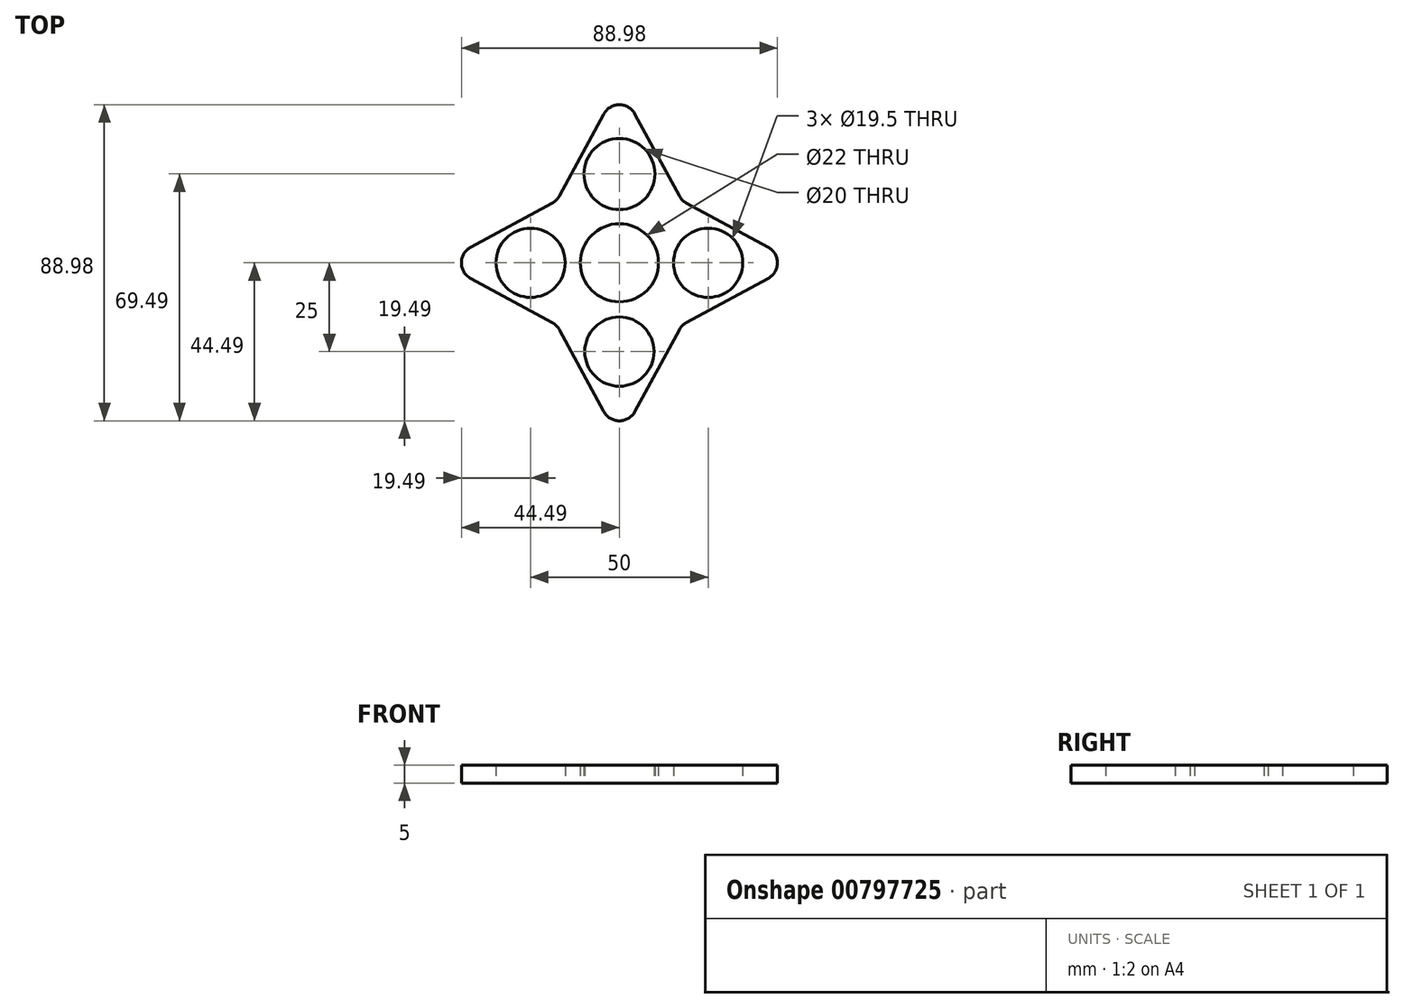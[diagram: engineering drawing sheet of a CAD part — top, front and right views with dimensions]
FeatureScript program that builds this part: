
annotation { "Feature Type Name" : "Feature", "Feature Type Description" : "" }
export const myFeature = defineFeature(function(context is Context, id is Id, definition is map)
    precondition{}
    {
        {
            var Q0;
            Q0=qCreatedBy(makeId("Top.planeOp"),FACE);
            var sketch = newSketch(context, id + "F0", { "sketchPlane" : qUnion([Q0])});
            skCircle(sketch, "E0", {"center": v(0, 0) * mm, "radius": 11 * mm});
            skLineSegment(sketch, "E1", {"start": v(0, 50) * mm, "end": v(-17.56, 17.56) * mm});
            skLineSegment(sketch, "E2", {"start": v(0, 50) * mm, "end": v(17.56, 17.56) * mm});
            skCircle(sketch, "E3", {"center": v(0, 25) * mm, "radius": 10 * mm});
            skLineSegment(sketch, "E4.1.1", {"start": v(-50, 0) * mm, "end": v(-17.56, -17.56) * mm});
            skCircle(sketch, "E4.1.2", {"center": v(-25, 0) * mm, "radius": 9.75 * mm});
            skLineSegment(sketch, "E4.1.4", {"start": v(-50, 0) * mm, "end": v(-17.56, 17.56) * mm});
            skLineSegment(sketch, "E4.2.1", {"start": v(0, -50) * mm, "end": v(17.56, -17.56) * mm});
            skCircle(sketch, "E4.2.2", {"center": v(0, -25) * mm, "radius": 9.75 * mm});
            skLineSegment(sketch, "E4.2.4", {"start": v(0, -50) * mm, "end": v(-17.56, -17.56) * mm});
            skLineSegment(sketch, "E4.3.1", {"start": v(50, 0) * mm, "end": v(17.56, 17.56) * mm});
            skCircle(sketch, "E4.3.2", {"center": v(25, 0) * mm, "radius": 9.75 * mm});
            skLineSegment(sketch, "E4.3.4", {"start": v(50, 0) * mm, "end": v(17.56, -17.56) * mm});
            skPoint(sketch, "E5.orphan", {"position": v(0, -15.25) * mm});
            skSolve(sketch);
        }
        {
            var Q0;
            Q0=makeQuery(id+"F0.imprint","IMPRINT",FACE,{"disambiguationData":[TD([[makeQuery(id+"F0.imprint","IMPRINT",EDGE,{"derivedFrom":sQuery(id+"F0.wireOp",EDGE,"E1")}),1.0]])]});
            extrude(context, id + "F1", {"entities" : qUnion([Q0]), "depth" : 5 * mm, "offsetDistance" : 25 * mm});
        }
        {
            var Q0;
            Q0=makeQuery(id+"F1.opExtrude","SWEPT_EDGE",EDGE,{"disambiguationData":[OSD([sQuery(id+"F0.wireOp",EDGE,"E4.2.1"),sQuery(id+"F0.wireOp",EDGE,"E4.2.4")])]});
            var Q1;
            Q1=makeQuery(id+"F1.opExtrude","SWEPT_EDGE",EDGE,{"disambiguationData":[OSD([sQuery(id+"F0.wireOp",EDGE,"E4.3.1"),sQuery(id+"F0.wireOp",EDGE,"E4.3.4")])]});
            var Q2;
            Q2=makeQuery(id+"F1.opExtrude","SWEPT_EDGE",EDGE,{"disambiguationData":[OSD([sQuery(id+"F0.wireOp",EDGE,"E1"),sQuery(id+"F0.wireOp",EDGE,"E2")])]});
            var Q3;
            Q3=makeQuery(id+"F1.opExtrude","SWEPT_EDGE",EDGE,{"disambiguationData":[OSD([sQuery(id+"F0.wireOp",EDGE,"E4.1.1"),sQuery(id+"F0.wireOp",EDGE,"E4.1.4")])]});
            var Q4;
            Q4=makeQuery(id+"F1.opExtrude","SWEPT_EDGE",EDGE,{"disambiguationData":[OSD([sQuery(id+"F0.wireOp",EDGE,"E2"),sQuery(id+"F0.wireOp",EDGE,"E4.3.1")])]});
            var Q5;
            Q5=makeQuery(id+"F1.opExtrude","SWEPT_EDGE",EDGE,{"disambiguationData":[OSD([sQuery(id+"F0.wireOp",EDGE,"E1"),sQuery(id+"F0.wireOp",EDGE,"E4.1.4")])]});
            var Q6;
            Q6=makeQuery(id+"F1.opExtrude","SWEPT_EDGE",EDGE,{"disambiguationData":[OSD([sQuery(id+"F0.wireOp",EDGE,"E4.1.1"),sQuery(id+"F0.wireOp",EDGE,"E4.2.4")])]});
            var Q7;
            Q7=makeQuery(id+"F1.opExtrude","SWEPT_EDGE",EDGE,{"disambiguationData":[OSD([sQuery(id+"F0.wireOp",EDGE,"E4.2.1"),sQuery(id+"F0.wireOp",EDGE,"E4.3.4")])]});
            fillet(context, id + "F2", {"entities" : qUnion([Q0, Q1, Q2, Q3, Q4, Q5, Q6, Q7]), "radius" : 5 * mm, "tangentPropagation" : true, "allowEdgeOverflow" : false});
        }
    });
